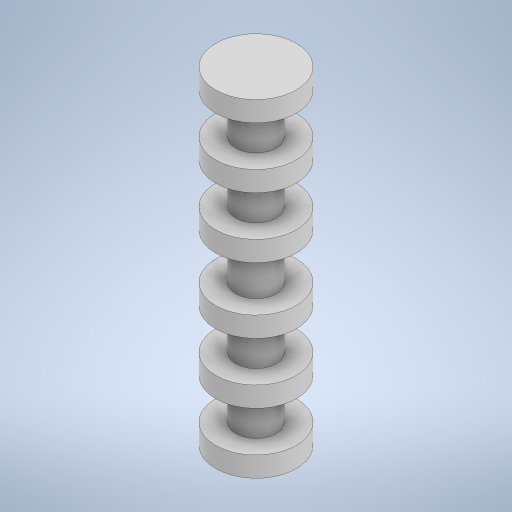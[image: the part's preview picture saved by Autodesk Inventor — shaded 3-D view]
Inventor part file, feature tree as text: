
AUTODESK INVENTOR PART (.ipt)
format: ipt  version: 2023 (Build 270158000, 158)  size: 293,376 bytes
history: native  units: in
note: dims shown in document units (in); Inventor stores cm internally (conversion verified against a paired STEP export)
features: revolve x1, sketch x1
ambient origin geometry x8: Origin, YZ Plane, XZ Plane, XY Plane, X Axis, Y Axis, Z Axis, Center Point
bodies: Solid1 (feature_tree)
feature tree (2):
  revolve  "Revolution1"  [1 undecoded]
  sketch  "Sketch1"  dims[d1=0.157in d2=0.093in d3=0.125in d4=0.25in d5=0.125in d6=0.25in d7=0.125in d8=0.1405in d9=90.0deg]
note: 1 required parameter value undecoded (feature->parameter linkage not recoverable at this tier; creation-order binding heuristic only, values carry confidence <= 0.55)
